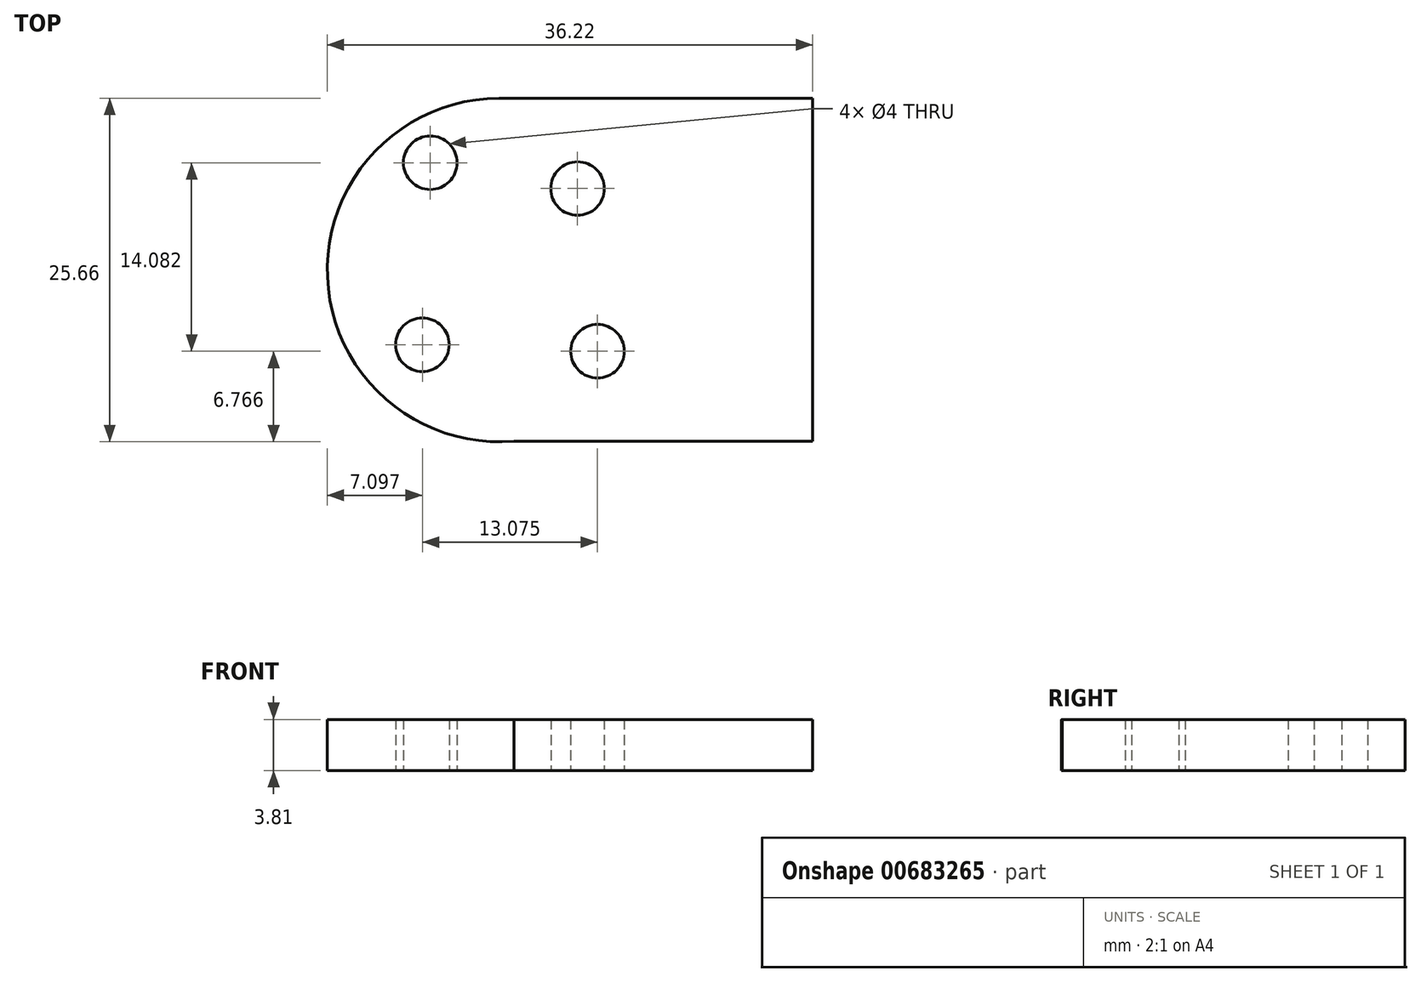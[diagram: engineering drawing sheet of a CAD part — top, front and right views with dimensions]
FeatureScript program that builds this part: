
annotation { "Feature Type Name" : "Feature", "Feature Type Description" : "" }
export const myFeature = defineFeature(function(context is Context, id is Id, definition is map)
    precondition{}
    {
        {
            var Q0;
            Q0=qCreatedBy(makeId("Top.planeOp"),FACE);
            var sketch = newSketch(context, id + "F0", { "sketchPlane" : qUnion([Q0])});
            skArc(sketch, "E0.MirrorCS", {"start": v(-34.06, 38.53) * mm, "mid": v(-46.88, 25.16) * mm, "end": v(-32.97, 12.92) * mm});
            skCircle(sketch, "E1", {"center": v(-26.72, 19.64) * mm, "radius": 2 * mm});
            skCircle(sketch, "E2", {"center": v(-39.2, 33.72) * mm, "radius": 2 * mm});
            skCircle(sketch, "E3", {"center": v(-39.8, 20.12) * mm, "radius": 2 * mm});
            skCircle(sketch, "E4", {"center": v(-28.21, 31.8) * mm, "radius": 2 * mm});
            skLineSegment(sketch, "E5", {"start": v(-34.06, 38.53) * mm, "end": v(-10.67, 38.53) * mm});
            skLineSegment(sketch, "E6", {"start": v(-10.67, 12.92) * mm, "end": v(-10.67, 38.53) * mm});
            skLineSegment(sketch, "E7", {"start": v(-32.97, 12.92) * mm, "end": v(-10.67, 12.92) * mm});
            skSolve(sketch);
        }
        {
            var Q0;
            Q0=makeQuery(id+"F0.imprint","IMPRINT",FACE,{"disambiguationData":[TD([[makeQuery(id+"F0.imprint","IMPRINT",EDGE,{"derivedFrom":sQuery(id+"F0.wireOp",EDGE,"E0.MirrorCS")}),1.0]])]});
            extrude(context, id + "F1", {"entities" : qUnion([Q0]), "depth" : 3.8 * mm, "offsetDistance" : 25.4 * mm});
        }
    });
